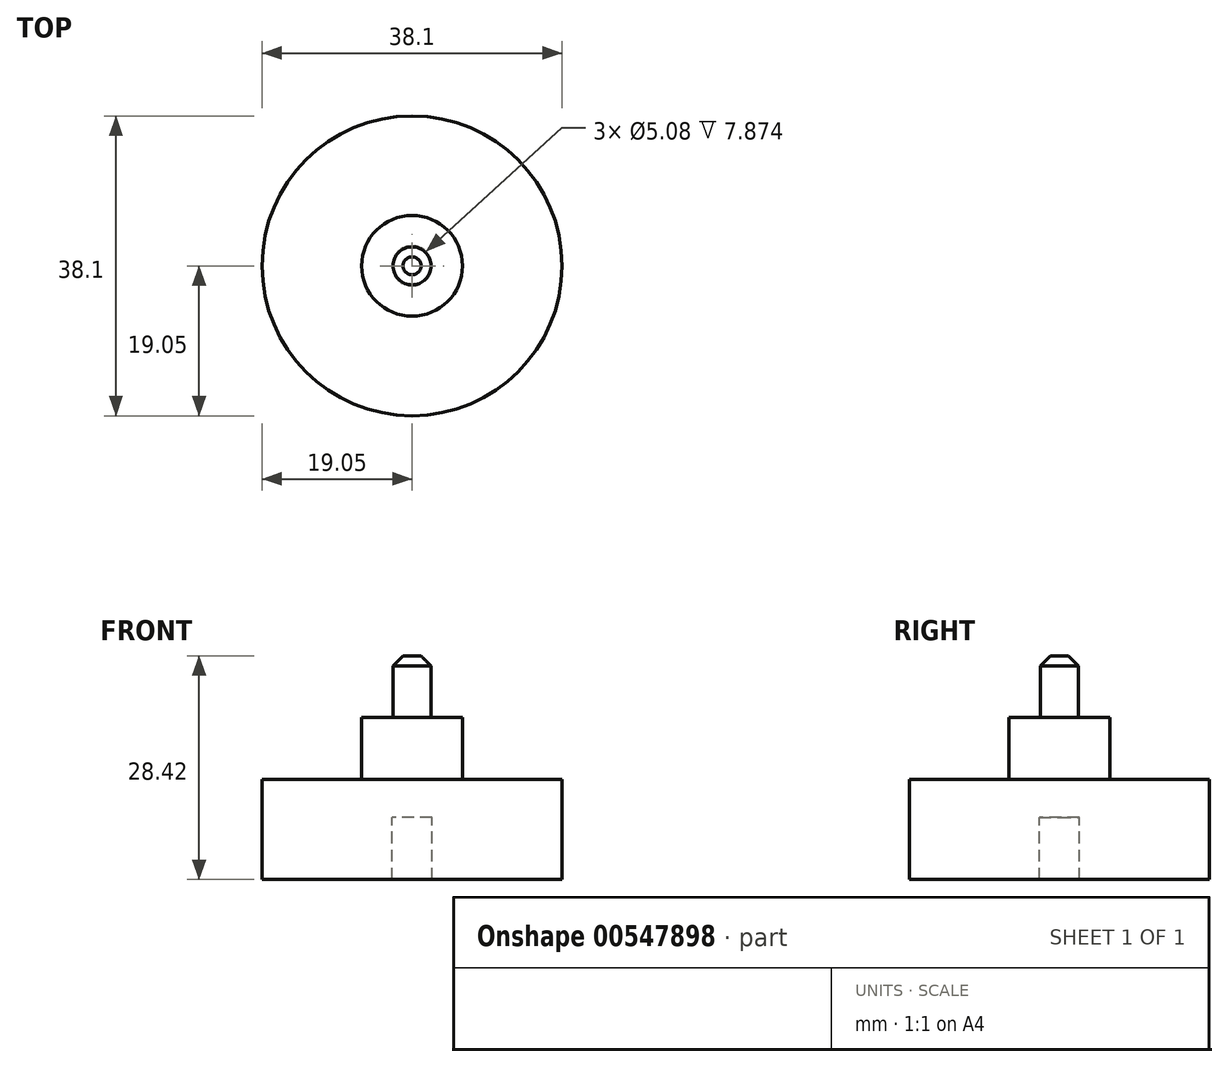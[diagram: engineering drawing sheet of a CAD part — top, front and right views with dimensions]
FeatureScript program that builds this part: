
annotation { "Feature Type Name" : "Feature", "Feature Type Description" : "" }
export const myFeature = defineFeature(function(context is Context, id is Id, definition is map)
    precondition{}
    {
        {
            var Q0;
            Q0=qCreatedBy(makeId("Front.planeOp"),FACE);
            var sketch = newSketch(context, id + "F0", { "sketchPlane" : qUnion([Q0])});
            skLineSegment(sketch, "E0", {"start": v(0, 0) * mm, "end": v(19.05, 0) * mm});
            skLineSegment(sketch, "E1", {"start": v(19.05, 0) * mm, "end": v(19.05, 12.7) * mm});
            skLineSegment(sketch, "E2", {"start": v(19.05, 12.7) * mm, "end": v(6.4, 12.7) * mm});
            skLineSegment(sketch, "E3", {"start": v(2.41, 20.57) * mm, "end": v(6.4, 20.57) * mm});
            skLineSegment(sketch, "E4", {"start": v(6.4, 20.57) * mm, "end": v(6.4, 12.7) * mm});
            skPoint(sketch, "E5.start.orphan", {"position": v(0, 12.7) * mm});
            skLineSegment(sketch, "E6", {"start": v(0, 28.42) * mm, "end": v(2.41, 28.42) * mm});
            skLineSegment(sketch, "E7", {"start": v(2.41, 28.42) * mm, "end": v(2.41, 20.57) * mm});
            skLineSegment(sketch, "E8", {"start": v(0, 0) * mm, "end": v(2.54, 0) * mm});
            skLineSegment(sketch, "E9", {"start": v(2.54, 0) * mm, "end": v(2.54, 7.87) * mm});
            skLineSegment(sketch, "E10", {"start": v(2.54, 7.87) * mm, "end": v(0, 7.87) * mm});
            skLineSegment(sketch, "E11", {"start": v(0, 28.42) * mm, "end": v(0, 7.87) * mm});
            skSolve(sketch);
        }
        {
            var Q0;
            Q0 = qSketchRegion(id + "F0", true);
            var Q1;
            Q1=sQuery(id+"F0.wireOp",EDGE,"E11");
            revolve(context, id + "F1", {"entities" : qUnion([Q0]), "axis" : qUnion([Q1]), "revolveType" : RevolveType.FULL});
        }
        {
            var Q0;
            Q0=makeQuery(id+"F1.opRevolve","SWEPT_EDGE",EDGE,{"disambiguationData":[OSD([sQuery(id+"F0.wireOp",EDGE,"E6"),sQuery(id+"F0.wireOp",EDGE,"E7")])]});
            chamfer(context, id + "F2", {"entities" : qUnion([Q0]), "width" : 1.27 * mm, "tangentPropagation" : true});
        }
    });
